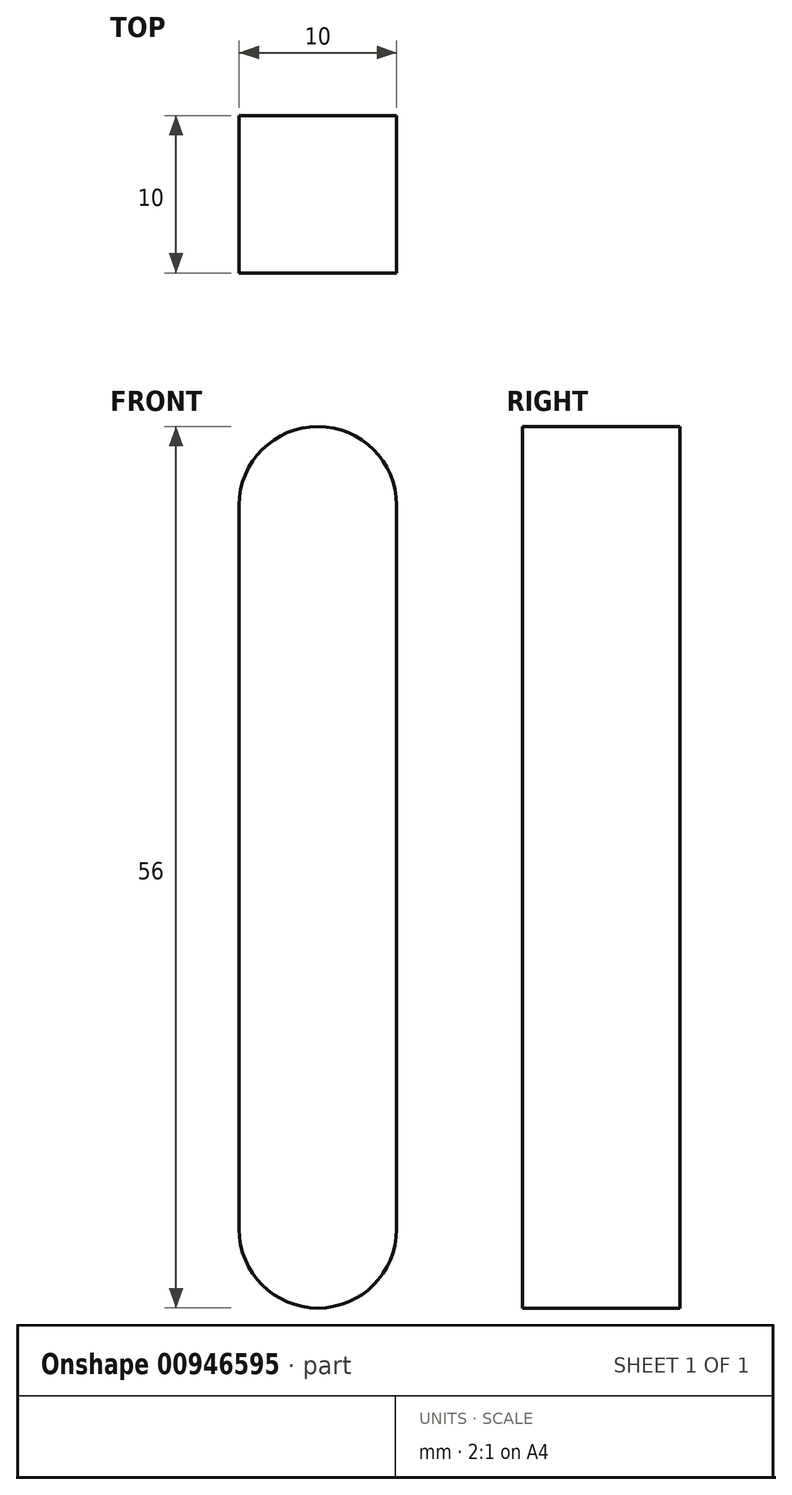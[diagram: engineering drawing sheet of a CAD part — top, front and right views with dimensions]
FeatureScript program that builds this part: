
annotation { "Feature Type Name" : "Feature", "Feature Type Description" : "" }
export const myFeature = defineFeature(function(context is Context, id is Id, definition is map)
    precondition{}
    {
        {
            var Q0;
            Q0=qCreatedBy(makeId("Front.planeOp"),FACE);
            var sketch = newSketch(context, id + "F0", { "sketchPlane" : qUnion([Q0])});
            skLineSegment(sketch, "E0", {"start": v(0, 16.52) * mm, "end": v(0, -29.48) * mm, "construction": true});
            skArc(sketch, "E1.0.startCap", {"start": v(-5, 16.52) * mm, "mid": v(0, 21.52) * mm, "end": v(5, 16.52) * mm});
            skArc(sketch, "E1.0.endCap", {"start": v(5, -29.48) * mm, "mid": v(0, -34.48) * mm, "end": v(-5, -29.48) * mm});
            skLineSegment(sketch, "E1.0.left", {"start": v(5, 16.52) * mm, "end": v(5, -29.48) * mm});
            skLineSegment(sketch, "E1.0.right", {"start": v(-5, 16.52) * mm, "end": v(-5, -29.48) * mm});
            skSolve(sketch);
        }
        {
            var Q0;
            Q0 = qSketchRegion(id + "F0", true);
            extrude(context, id + "F1", {"entities" : qUnion([Q0]), "depth" : 10 * mm, "offsetDistance" : 25 * mm});
        }
    });
